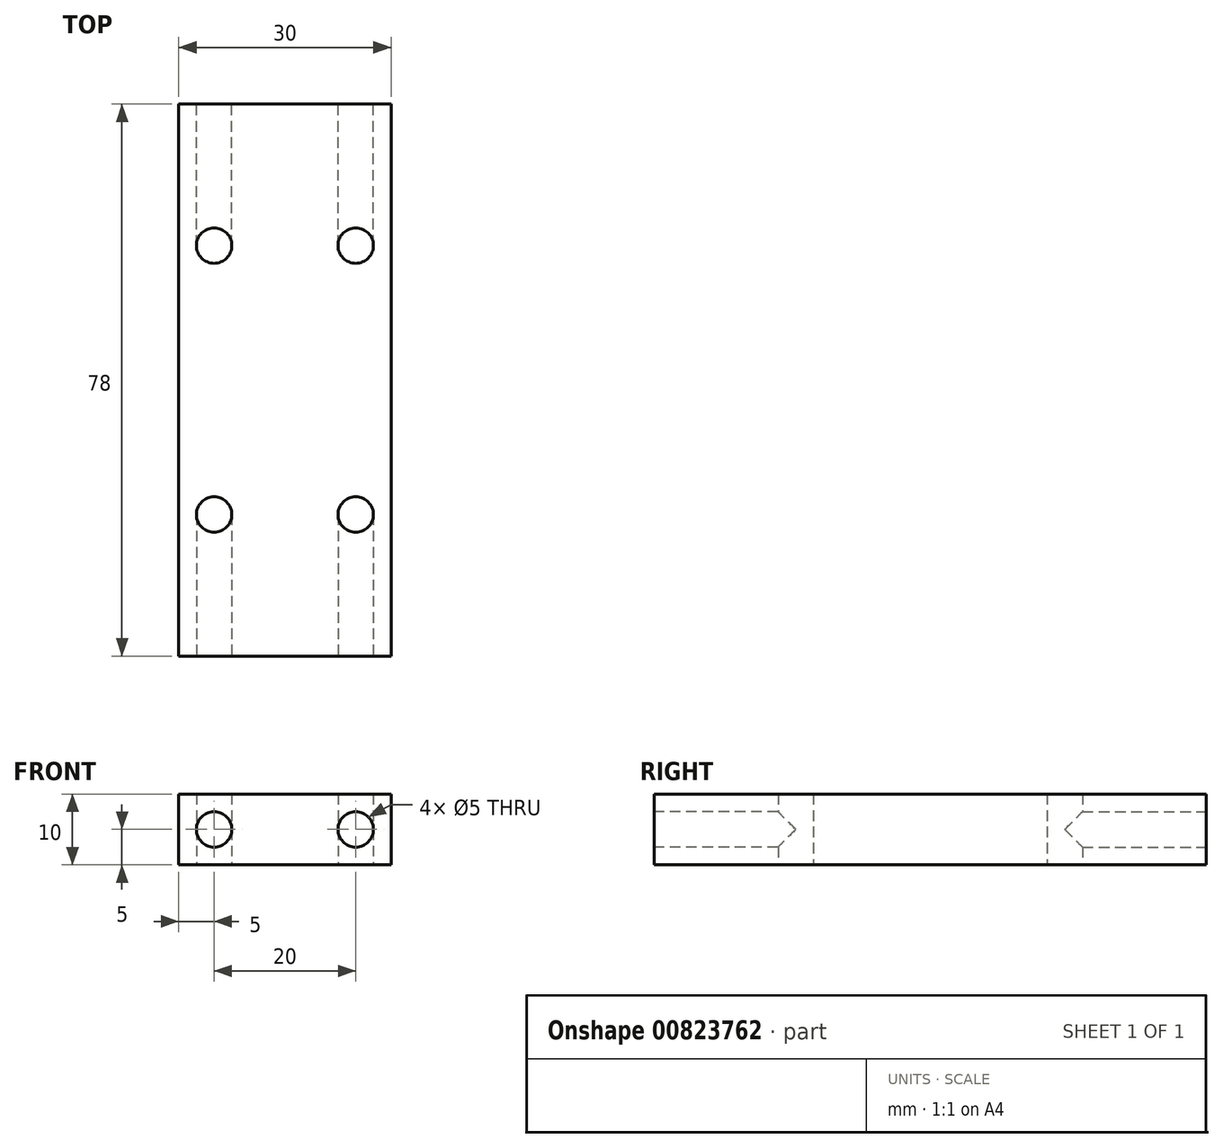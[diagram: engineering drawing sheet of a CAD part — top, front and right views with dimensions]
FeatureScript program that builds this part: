
annotation { "Feature Type Name" : "Feature", "Feature Type Description" : "" }
export const myFeature = defineFeature(function(context is Context, id is Id, definition is map)
    precondition{}
    {
        {
            var Q0;
            Q0=qCreatedBy(makeId("Top.planeOp"),FACE);
            var sketch = newSketch(context, id + "F0", { "sketchPlane" : qUnion([Q0])});
            skLineSegment(sketch, "E0.bottom", {"start": v(15, 39) * mm, "end": v(-15, 39) * mm});
            skLineSegment(sketch, "E0.top", {"start": v(15, -39) * mm, "end": v(-15, -39) * mm});
            skLineSegment(sketch, "E0.left", {"start": v(15, 39) * mm, "end": v(15, -39) * mm});
            skLineSegment(sketch, "E0.right", {"start": v(-15, 39) * mm, "end": v(-15, -39) * mm});
            skPoint(sketch, "E0.middle", {"position": v(0, 0) * mm});
            skPoint(sketch, "E1.centerSnap0", {"position": v(15, 0) * mm});
            skPoint(sketch, "E2.centerSnap0", {"position": v(-15, 0) * mm});
            skPoint(sketch, "E3.centerSnap0", {"position": v(0, -39) * mm});
            skPoint(sketch, "E4.centerSnap0", {"position": v(0, 39) * mm});
            skCircle(sketch, "E5", {"center": v(-10, -19) * mm, "radius": 2.5 * mm});
            skCircle(sketch, "E6", {"center": v(-10, 19) * mm, "radius": 2.5 * mm});
            skCircle(sketch, "E7", {"center": v(10, -19) * mm, "radius": 2.5 * mm});
            skCircle(sketch, "E8", {"center": v(10, 19) * mm, "radius": 2.5 * mm});
            skSolve(sketch);
        }
        {
            var Q0;
            Q0=makeQuery(id+"F0.imprint","IMPRINT",FACE,{"disambiguationData":[TD([[makeQuery(id+"F0.imprint","IMPRINT",EDGE,{"derivedFrom":sQuery(id+"F0.wireOp",EDGE,"E0.bottom")}),1.0]])]});
            extrude(context, id + "F1", {"entities" : qUnion([Q0]), "depth" : 10 * mm, "offsetDistance" : 25 * mm});
        }
        {
            var Q0;
            Q0=makeQuery(id+"F1.opExtrude","SWEPT_FACE",FACE,{"disambiguationData":[OSD([sQuery(id+"F0.wireOp",EDGE,"E0.top")])]});
            var sketch = newSketch(context, id + "F2", { "sketchPlane" : qUnion([Q0])});
            skCircle(sketch, "E9", {"center": v(-10, 5) * mm, "radius": 2.5 * mm});
            skPoint(sketch, "E9.centerSnap0", {"position": v(-15, 5) * mm});
            skCircle(sketch, "E10", {"center": v(10, 5) * mm, "radius": 2.5 * mm});
            skPoint(sketch, "E10.centerSnap0", {"position": v(15, 5) * mm});
            skSolve(sketch);
        }
        {
            var Q0;
            Q0 = qSketchRegion(id + "F2", true);
            extrude(context, id + "F3", {"entities" : qUnion([Q0]), "operationType" : NewBodyOperationType.REMOVE, "oppositeDirection" : true, "depth" : 20 * mm, "offsetDistance" : 25 * mm});
        }
        {
            var Q0;
            Q0=makeQuery(id+"F1.opExtrude","SWEPT_FACE",FACE,{"disambiguationData":[OSD([sQuery(id+"F0.wireOp",EDGE,"E0.bottom")])]});
            var sketch = newSketch(context, id + "F4", { "sketchPlane" : qUnion([Q0])});
            skCircle(sketch, "E11", {"center": v(-10, 5) * mm, "radius": 2.5 * mm});
            skPoint(sketch, "E11.centerSnap0", {"position": v(-15, 5) * mm});
            skCircle(sketch, "E12", {"center": v(10, 5) * mm, "radius": 2.5 * mm});
            skPoint(sketch, "E12.centerSnap0", {"position": v(15, 5) * mm});
            skSolve(sketch);
        }
        {
            var Q0;
            Q0 = qSketchRegion(id + "F4", true);
            extrude(context, id + "F5", {"entities" : qUnion([Q0]), "operationType" : NewBodyOperationType.REMOVE, "oppositeDirection" : true, "depth" : 20 * mm, "offsetDistance" : 25 * mm});
        }
    });
